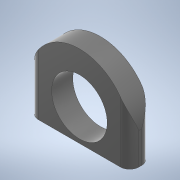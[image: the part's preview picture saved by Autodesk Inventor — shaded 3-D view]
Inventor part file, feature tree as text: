
AUTODESK INVENTOR PART (.ipt)
format: ipt  version: 2020 (Build 240168000, 168)  size: 179,712 bytes
history: native  units: mm
features: projected_geometry x9, sketch x5, extrude x4, other x1, fillet x1
ambient origin geometry x8: Origin, YZ Plane, XZ Plane, XY Plane, X Axis, Y Axis, Z Axis, Center Point
bodies: Body1 (feature_tree)
feature tree (20):
  other  "Твердое тело1"
  sketch  "Эскиз1"
  extrude  "Выдавливание1"  Depth=30.0mm
  fillet  "Сопряжение1"  Radius=4.0mm
  extrude  "Выдавливание2"  Depth=38.0mm
  extrude  "Выдавливание3"  Depth=8.0mm
  extrude  "Выдавливание4"  Depth=35.0mm TaperAngle=0.0deg
  sketch  "Эскиз2"
  sketch  "Эскиз3"
  projected_geometry  "Спроецированная петля1"
  projected_geometry  "Спроецированная петля2"
  projected_geometry  "Спроецированная петля3"
  projected_geometry  "Спроецированная петля4"
  projected_geometry  "Спроецированная петля5"
  projected_geometry  "Спроецированная петля6"
  sketch  "Эскиз4"
  projected_geometry  "Спроецированная петля7"
  projected_geometry  "Спроецированная петля8"
  projected_geometry  "Спроецированная петля9"
  sketch  "Эскиз5"
